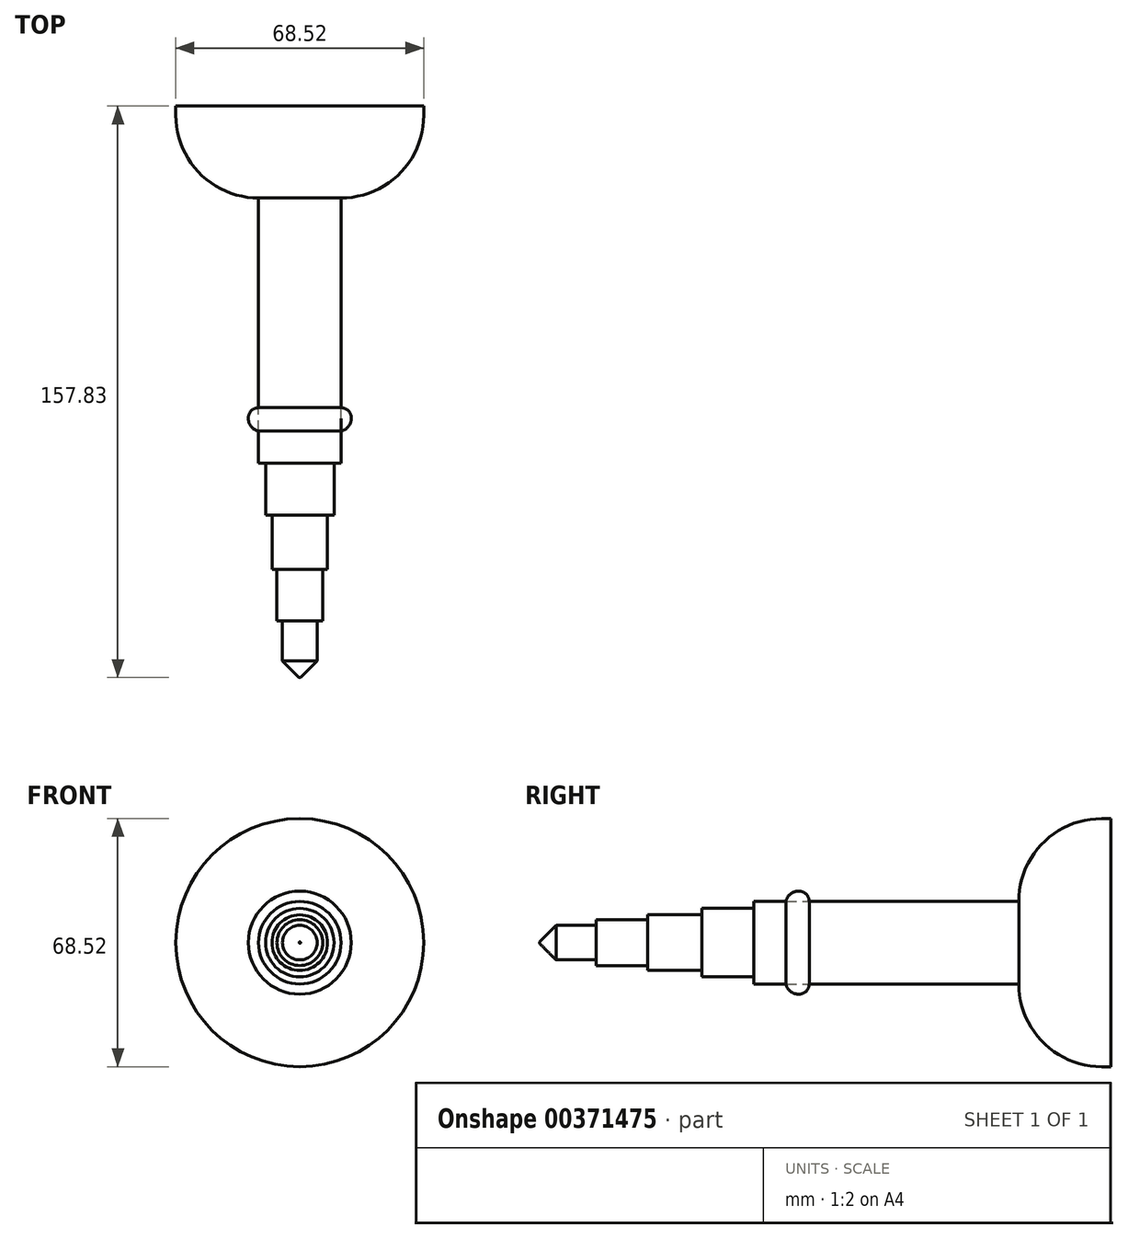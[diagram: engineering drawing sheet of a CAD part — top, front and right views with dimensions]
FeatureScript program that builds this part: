
annotation { "Feature Type Name" : "Feature", "Feature Type Description" : "" }
export const myFeature = defineFeature(function(context is Context, id is Id, definition is map)
    precondition{}
    {
        {
            var Q0;
            Q0=qCreatedBy(makeId("Front.planeOp"),FACE);
            var sketch = newSketch(context, id + "F0", { "sketchPlane" : qUnion([Q0])});
            skCircle(sketch, "E0", {"center": v(0, 0) * mm, "radius": 34.26 * mm});
            skSolve(sketch);
        }
        {
            var Q0;
            Q0 = qSketchRegion(id + "F0", true);
            extrude(context, id + "F1", {"entities" : qUnion([Q0]), "depth" : 25.4 * mm});
        }
        {
            var Q0;
            Q0=makeQuery(id+"F1.opExtrude","CAP_EDGE",EDGE,{"disambiguationData":[OSD([sQuery(id+"F0.wireOp",EDGE,"E0")])],"isStart":false});
            fillet(context, id + "F2", {"entities" : qUnion([Q0]), "radius" : 22.86 * mm, "tangentPropagation" : true, "allowEdgeOverflow" : false});
        }
        {
            var Q0;
            Q0=makeQuery(id+"F1.opExtrude","CAP_FACE",FACE,{"disambiguationData":[OSD([sQuery(id+"F0.wireOp",EDGE,"E0")])],"isStart":false});
            extrude(context, id + "F3", {"entities" : qUnion([Q0]), "operationType" : NewBodyOperationType.ADD, "depth" : 57.92 * mm});
        }
        {
            var Q0;
            Q0=makeQuery(id+"F3.opExtrude","CAP_FACE",FACE,{"disambiguationData":[OSD([sQuery(id+"F0.wireOp",EDGE,"E0")])],"isStart":false});
            var sketch = newSketch(context, id + "F4", { "sketchPlane" : qUnion([Q0])});
            skCircle(sketch, "E1", {"center": v(0, 0) * mm, "radius": 14.22 * mm});
            skSolve(sketch);
        }
        {
            var Q0;
            Q0=makeQuery(id+"F4.imprint","IMPRINT",FACE,{"disambiguationData":[TD([[makeQuery(id+"F4.imprint","IMPRINT",EDGE,{"derivedFrom":sQuery(id+"F4.wireOp",EDGE,"E1")}),1.0]])]});
            extrude(context, id + "F5", {"entities" : qUnion([Q0]), "depth" : 6.46 * mm});
        }
        {
            var Q0;
            Q0=makeQuery(id+"F5.opExtrude","CAP_EDGE",EDGE,{"disambiguationData":[OSD([sQuery(id+"F4.wireOp",EDGE,"E1")])],"isStart":false});
            fillet(context, id + "F6", {"entities" : qUnion([Q0]), "radius" : 3.56 * mm, "tangentPropagation" : true, "allowEdgeOverflow" : false});
        }
        {
            var Q0;
            Q0=makeQuery(id+"F5.opExtrude","CAP_EDGE",EDGE,{"disambiguationData":[OSD([sQuery(id+"F4.wireOp",EDGE,"E1")])],"isStart":true});
            fillet(context, id + "F7", {"entities" : qUnion([Q0]), "radius" : 2.8 * mm, "tangentPropagation" : true, "allowEdgeOverflow" : false});
        }
        {
            var Q0;
            Q0=makeQuery(id+"F3.opExtrude","CAP_FACE",FACE,{"disambiguationData":[OSD([sQuery(id+"F0.wireOp",EDGE,"E0")])],"isStart":false});
            extrude(context, id + "F8", {"entities" : qUnion([Q0]), "depth" : 15.27 * mm});
        }
        {
            var Q0;
            Q0=makeQuery(id+"F8.opExtrude","CAP_FACE",FACE,{"disambiguationData":[OSD([sQuery(id+"F0.wireOp",EDGE,"E0")])],"isStart":false});
            var sketch = newSketch(context, id + "F9", { "sketchPlane" : qUnion([Q0])});
            skCircle(sketch, "E2", {"center": v(0, 0) * mm, "radius": 9.46 * mm});
            skSolve(sketch);
        }
        {
            var Q0;
            Q0=makeQuery(id+"F9.imprint","IMPRINT",FACE,{"disambiguationData":[TD([[makeQuery(id+"F9.imprint","IMPRINT",EDGE,{"derivedFrom":sQuery(id+"F9.wireOp",EDGE,"E2")}),1.0]])]});
            extrude(context, id + "F10", {"entities" : qUnion([Q0]), "operationType" : NewBodyOperationType.ADD, "depth" : 14.37 * mm});
        }
        {
            var Q0;
            Q0=makeQuery(id+"F10.opExtrude","CAP_FACE",FACE,{"disambiguationData":[OSD([sQuery(id+"F9.wireOp",EDGE,"E2")])],"isStart":false});
            var sketch = newSketch(context, id + "F11", { "sketchPlane" : qUnion([Q0])});
            skCircle(sketch, "E3", {"center": v(0, 0) * mm, "radius": 7.67 * mm});
            skSolve(sketch);
        }
        {
            var Q0;
            Q0=makeQuery(id+"F11.imprint","IMPRINT",FACE,{"disambiguationData":[TD([[makeQuery(id+"F11.imprint","IMPRINT",EDGE,{"derivedFrom":sQuery(id+"F11.wireOp",EDGE,"E3")}),1.0]])]});
            extrude(context, id + "F12", {"entities" : qUnion([Q0]), "operationType" : NewBodyOperationType.ADD, "depth" : 15.04 * mm});
        }
        {
            var Q0;
            Q0=makeQuery(id+"F12.opExtrude","CAP_FACE",FACE,{"disambiguationData":[OSD([sQuery(id+"F11.wireOp",EDGE,"E3")])],"isStart":false});
            var sketch = newSketch(context, id + "F13", { "sketchPlane" : qUnion([Q0])});
            skCircle(sketch, "E4", {"center": v(0, 0) * mm, "radius": 6.32 * mm});
            skSolve(sketch);
        }
        {
            var Q0;
            Q0=makeQuery(id+"F13.imprint","IMPRINT",FACE,{"disambiguationData":[TD([[makeQuery(id+"F13.imprint","IMPRINT",EDGE,{"derivedFrom":sQuery(id+"F13.wireOp",EDGE,"E4")}),1.0]])]});
            extrude(context, id + "F14", {"entities" : qUnion([Q0]), "operationType" : NewBodyOperationType.ADD, "depth" : 14.23 * mm});
        }
        {
            var Q0;
            Q0=makeQuery(id+"F14.opExtrude","CAP_FACE",FACE,{"disambiguationData":[OSD([sQuery(id+"F13.wireOp",EDGE,"E4")])],"isStart":false});
            var sketch = newSketch(context, id + "F15", { "sketchPlane" : qUnion([Q0])});
            skCircle(sketch, "E5", {"center": v(0, 0) * mm, "radius": 4.78 * mm});
            skSolve(sketch);
        }
        {
            var Q0;
            Q0=makeQuery(id+"F15.imprint","IMPRINT",FACE,{"disambiguationData":[TD([[makeQuery(id+"F15.imprint","IMPRINT",EDGE,{"derivedFrom":sQuery(id+"F15.wireOp",EDGE,"E5")}),1.0]])]});
            extrude(context, id + "F16", {"entities" : qUnion([Q0]), "operationType" : NewBodyOperationType.ADD, "depth" : 15.6 * mm});
        }
        {
            var Q0;
            Q0=makeQuery(id+"F16.opExtrude","CAP_EDGE",EDGE,{"disambiguationData":[OSD([sQuery(id+"F15.wireOp",EDGE,"E5")])],"isStart":false});
            chamfer(context, id + "F17", {"entities" : qUnion([Q0]), "width" : 4.57 * mm, "tangentPropagation" : true});
        }
    });
